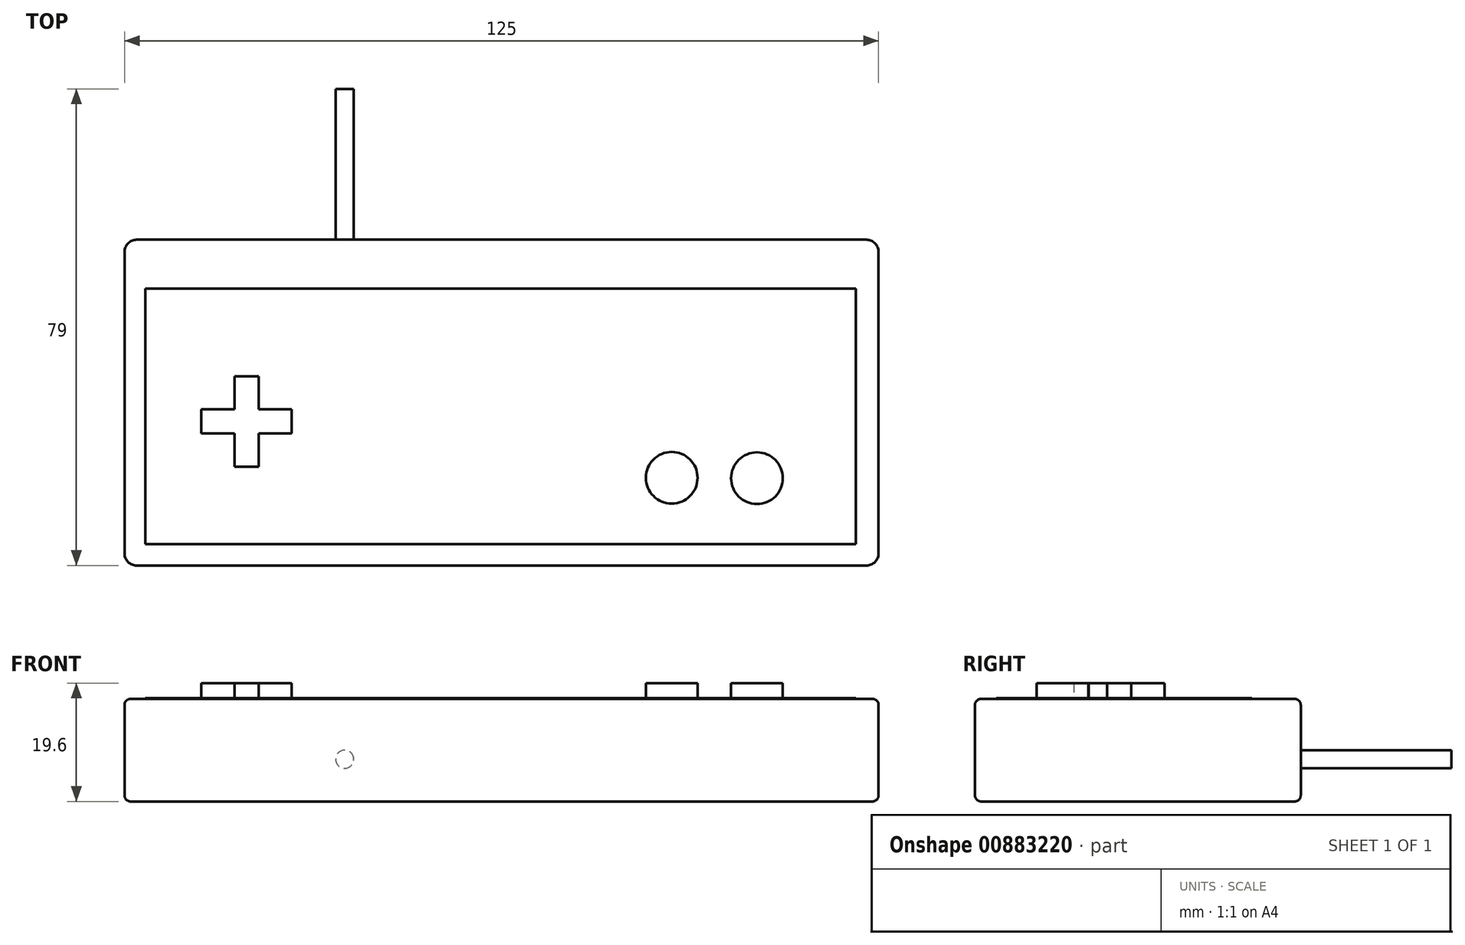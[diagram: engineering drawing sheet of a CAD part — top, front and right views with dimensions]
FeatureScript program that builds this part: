
annotation { "Feature Type Name" : "Feature", "Feature Type Description" : "" }
export const myFeature = defineFeature(function(context is Context, id is Id, definition is map)
    precondition{}
    {
        {
            var Q0;
            Q0=qCreatedBy(makeId("Top.planeOp"),FACE);
            var sketch = newSketch(context, id + "F0", { "sketchPlane" : qUnion([Q0])});
            skLineSegment(sketch, "E0.bottom", {"start": v(0, 0) * mm, "end": v(125, 0) * mm});
            skLineSegment(sketch, "E0.top", {"start": v(0, 54) * mm, "end": v(125, 54) * mm});
            skLineSegment(sketch, "E0.left", {"start": v(0, 0) * mm, "end": v(0, 54) * mm});
            skLineSegment(sketch, "E0.right", {"start": v(125, 0) * mm, "end": v(125, 54) * mm});
            skSolve(sketch);
        }
        {
            var Q0;
            Q0 = qSketchRegion(id + "F0", true);
            extrude(context, id + "F1", {"entities" : qUnion([Q0]), "depth" : 17 * mm, "offsetDistance" : 25 * mm});
        }
        {
            var Q0;
            Q0=makeQuery(id+"F1.opExtrude","SWEPT_EDGE",EDGE,{"disambiguationData":[OSD([sQuery(id+"F0.wireOp",EDGE,"E0.top"),sQuery(id+"F0.wireOp",EDGE,"E0.right")])]});
            var Q1;
            Q1=makeQuery(id+"F1.opExtrude","SWEPT_EDGE",EDGE,{"disambiguationData":[OSD([sQuery(id+"F0.wireOp",EDGE,"E0.bottom"),sQuery(id+"F0.wireOp",EDGE,"E0.right")])]});
            var Q2;
            Q2=makeQuery(id+"F1.opExtrude","SWEPT_EDGE",EDGE,{"disambiguationData":[OSD([sQuery(id+"F0.wireOp",EDGE,"E0.bottom"),sQuery(id+"F0.wireOp",EDGE,"E0.left")])]});
            var Q3;
            Q3=makeQuery(id+"F1.opExtrude","SWEPT_EDGE",EDGE,{"disambiguationData":[OSD([sQuery(id+"F0.wireOp",EDGE,"E0.top"),sQuery(id+"F0.wireOp",EDGE,"E0.left")])]});
            fillet(context, id + "F2", {"entities" : qUnion([Q0, Q1, Q2, Q3]), "radius" : 2 * mm, "tangentPropagation" : true, "allowEdgeOverflow" : false});
        }
        {
            var Q0;
            Q0=makeQuery(id+"F1.opExtrude","CAP_EDGE",EDGE,{"disambiguationData":[OSD([sQuery(id+"F0.wireOp",EDGE,"E0.bottom")])],"isStart":false});
            var Q1;
            Q1=makeQuery(id+"F1.opExtrude","CAP_EDGE",EDGE,{"disambiguationData":[OSD([sQuery(id+"F0.wireOp",EDGE,"E0.bottom")])],"isStart":true});
            fillet(context, id + "F3", {"entities" : qUnion([Q0, Q1]), "radius" : 1 * mm, "tangentPropagation" : true, "allowEdgeOverflow" : false});
        }
        {
            var Q0;
            Q0=makeQuery(id+"F1.opExtrude","CAP_FACE",FACE,{"disambiguationData":[OSD([sQuery(id+"F0.wireOp",EDGE,"E0.bottom"),sQuery(id+"F0.wireOp",EDGE,"E0.top"),sQuery(id+"F0.wireOp",EDGE,"E0.left"),sQuery(id+"F0.wireOp",EDGE,"E0.right")])],"isStart":false});
            var sketch = newSketch(context, id + "F4", { "sketchPlane" : qUnion([Q0])});
            skLineSegment(sketch, "E1.bottom", {"start": v(3.43, 45.87) * mm, "end": v(121.25, 45.87) * mm});
            skLineSegment(sketch, "E1.top", {"start": v(3.43, 3.57) * mm, "end": v(121.25, 3.57) * mm});
            skLineSegment(sketch, "E1.left", {"start": v(3.43, 45.87) * mm, "end": v(3.43, 3.57) * mm});
            skLineSegment(sketch, "E1.right", {"start": v(121.25, 45.87) * mm, "end": v(121.25, 3.57) * mm});
            skSolve(sketch);
        }
        {
            var Q0;
            Q0 = qSketchRegion(id + "F4", true);
            extrude(context, id + "F5", {"entities" : qUnion([Q0]), "depth" : 0.1 * mm, "offsetDistance" : 25 * mm});
        }
        {
            var Q0;
            Q0=makeQuery(id+"F5.opExtrude","CAP_FACE",FACE,{"disambiguationData":[OSD([sQuery(id+"F4.wireOp",EDGE,"E1.bottom"),sQuery(id+"F4.wireOp",EDGE,"E1.top"),sQuery(id+"F4.wireOp",EDGE,"E1.left"),sQuery(id+"F4.wireOp",EDGE,"E1.right")])],"isStart":false});
            var sketch = newSketch(context, id + "F6", { "sketchPlane" : qUnion([Q0])});
            skCircle(sketch, "E2", {"center": v(90.72, 14.55) * mm, "radius": 4.29 * mm});
            skCircle(sketch, "E3", {"center": v(104.85, 14.48) * mm, "radius": 4.29 * mm});
            skSolve(sketch);
        }
        {
            var Q0;
            Q0 = qSketchRegion(id + "F6", true);
            extrude(context, id + "F7", {"entities" : qUnion([Q0]), "depth" : 2.5 * mm, "offsetDistance" : 25 * mm});
        }
        {
            var Q0;
            Q0=makeQuery(id+"F5.opExtrude","CAP_FACE",FACE,{"disambiguationData":[OSD([sQuery(id+"F4.wireOp",EDGE,"E1.bottom"),sQuery(id+"F4.wireOp",EDGE,"E1.top"),sQuery(id+"F4.wireOp",EDGE,"E1.left"),sQuery(id+"F4.wireOp",EDGE,"E1.right")])],"isStart":false});
            var sketch = newSketch(context, id + "F8", { "sketchPlane" : qUnion([Q0])});
            skLineSegment(sketch, "E4.bottom", {"start": v(18.23, 31.4) * mm, "end": v(22.23, 31.4) * mm});
            skLineSegment(sketch, "E4.top", {"start": v(18.23, 16.4) * mm, "end": v(22.23, 16.4) * mm});
            skLineSegment(sketch, "E4.left", {"start": v(18.23, 31.4) * mm, "end": v(18.23, 16.4) * mm});
            skLineSegment(sketch, "E4.right", {"start": v(22.23, 31.4) * mm, "end": v(22.23, 16.4) * mm});
            skLineSegment(sketch, "E5.bottom", {"start": v(12.73, 25.9) * mm, "end": v(27.73, 25.9) * mm});
            skLineSegment(sketch, "E5.top", {"start": v(12.73, 21.9) * mm, "end": v(27.73, 21.9) * mm});
            skLineSegment(sketch, "E5.left", {"start": v(12.73, 25.9) * mm, "end": v(12.73, 21.9) * mm});
            skLineSegment(sketch, "E5.right", {"start": v(27.73, 25.9) * mm, "end": v(27.73, 21.9) * mm});
            skSolve(sketch);
        }
        {
            var Q0;
            Q0 = qSketchRegion(id + "F8", true);
            extrude(context, id + "F9", {"entities" : qUnion([Q0]), "depth" : 2.5 * mm, "offsetDistance" : 25 * mm});
        }
        {
            var Q0;
            Q0=makeQuery(id+"F1.opExtrude","SWEPT_FACE",FACE,{"disambiguationData":[OSD([sQuery(id+"F0.wireOp",EDGE,"E0.top")])]});
            var sketch = newSketch(context, id + "F10", { "sketchPlane" : qUnion([Q0])});
            skCircle(sketch, "E6", {"center": v(-36.5, 7) * mm, "radius": 1.5 * mm});
            skSolve(sketch);
        }
        {
            var Q0;
            Q0 = qSketchRegion(id + "F10", true);
            extrude(context, id + "F11", {"entities" : qUnion([Q0]), "operationType" : NewBodyOperationType.ADD, "depth" : 25 * mm, "offsetDistance" : 25 * mm});
        }
    });
